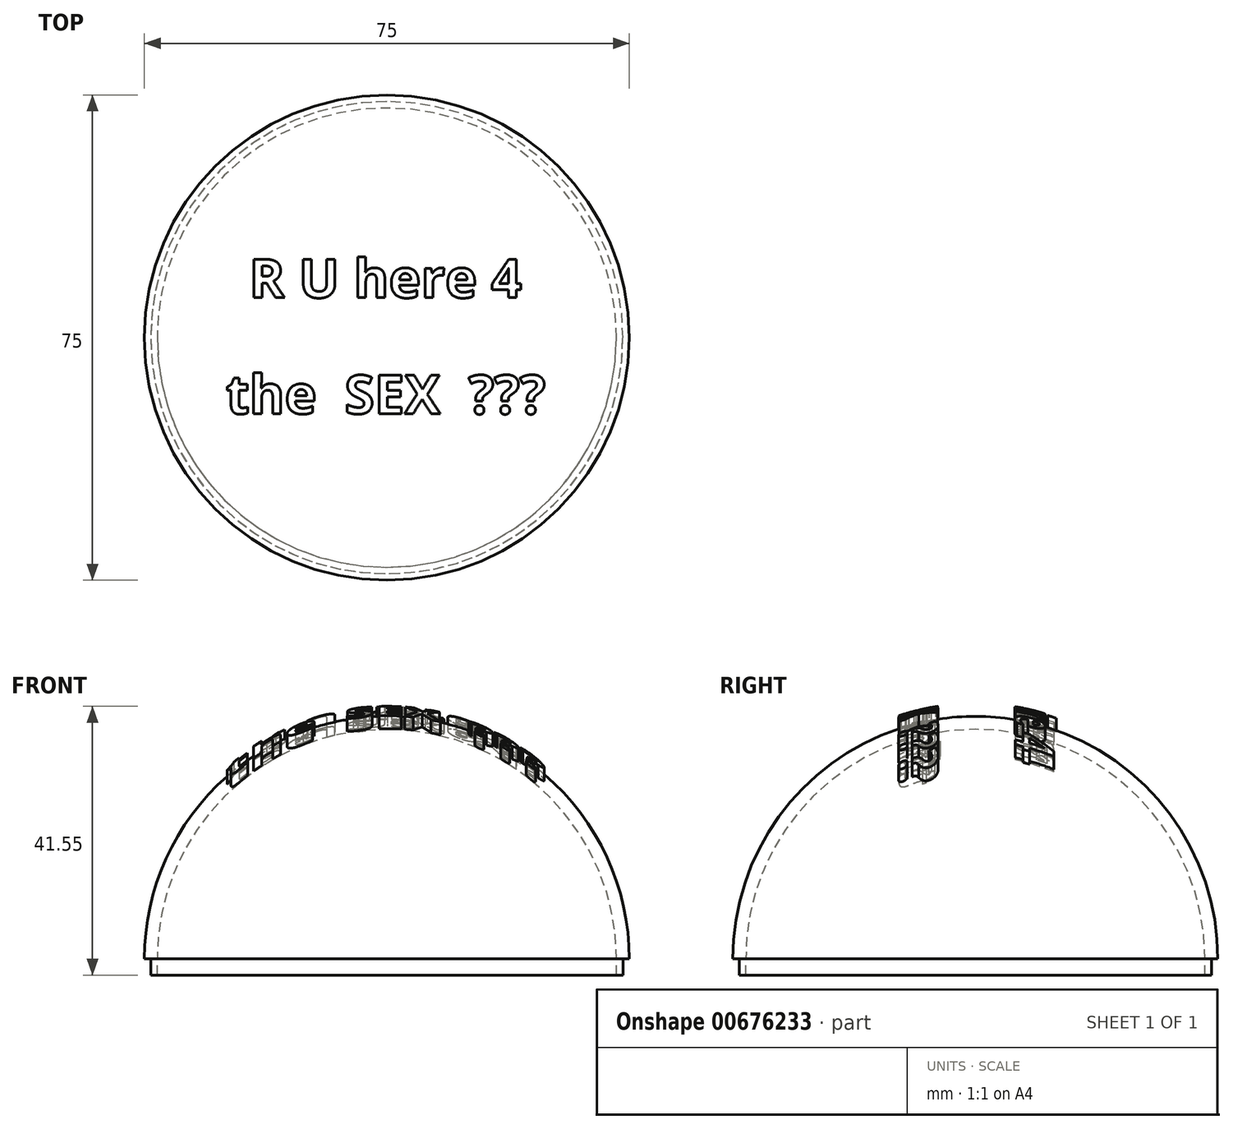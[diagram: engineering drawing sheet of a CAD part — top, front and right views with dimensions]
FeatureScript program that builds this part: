
annotation { "Feature Type Name" : "Feature", "Feature Type Description" : "" }
export const myFeature = defineFeature(function(context is Context, id is Id, definition is map)
    precondition{}
    {
        {
            var Q0;
            Q0=qCreatedBy(makeId("Front.planeOp"),FACE);
            var sketch = newSketch(context, id + "F0", { "sketchPlane" : qUnion([Q0])});
            skArc(sketch, "E0", {"start": v(37.5, 0) * mm, "mid": v(0, 37.5) * mm, "end": v(-37.5, 0) * mm});
            skArc(sketch, "E1", {"start": v(35.5, 0) * mm, "mid": v(0, 35.5) * mm, "end": v(-35.5, 0) * mm});
            skLineSegment(sketch, "E2", {"start": v(35.5, 0) * mm, "end": v(37.5, 0) * mm});
            skLineSegment(sketch, "E3", {"start": v(-37.5, 0) * mm, "end": v(-35.5, 0) * mm});
            skLineSegment(sketch, "E4", {"start": v(-37.5, 0) * mm, "end": v(42.78, 0) * mm, "construction": true});
            skLineSegment(sketch, "E5", {"start": v(36.5, 0) * mm, "end": v(36.5, 2.5) * mm});
            skLineSegment(sketch, "E6", {"start": v(36.5, 2.5) * mm, "end": v(35.41, 2.5) * mm});
            skLineSegment(sketch, "E7", {"start": v(36.5, 0) * mm, "end": v(36.5, -2.5) * mm});
            skLineSegment(sketch, "E8", {"start": v(36.5, -2.5) * mm, "end": v(35.5, -2.5) * mm});
            skLineSegment(sketch, "E9", {"start": v(35.5, 0) * mm, "end": v(35.5, -2.5) * mm});
            skSolve(sketch);
        }
        {
            var Q0;
            Q0=makeQuery(id+"F0.imprint","IMPRINT",FACE,{"disambiguationData":[TD([[makeQuery(id+"F0.imprint","IMPRINT",EDGE,{"derivedFrom":sQuery(id+"F0.wireOp",EDGE,"E0")}),1.0]])]});
            var Q1;
            {var subQ4=sQuery(id+"F0.wireOp",EDGE,"E5");Q1=makeQuery(id+"F0.imprint","IMPRINT",FACE,{"disambiguationData":[TD([[makeQuery(id+"F0.imprint","IMPRINT",EDGE,{"derivedFrom":subQ4}),1.0]])]});}
            var Q2;
            Q2=sQuery(id+"F0.wireOp",EDGE,"E4");
            revolve(context, id + "F1", {"entities" : qUnion([Q0, Q1]), "axis" : qUnion([Q2]), "revolveType" : RevolveType.SYMMETRIC, "angle" : 180 * degree});
        }
        {
            var Q0;
            Q0=qCreatedBy(makeId("Top.planeOp"),FACE);
            var sketch = newSketch(context, id + "F2", { "sketchPlane" : qUnion([Q0])});
            skText(sketch, "E10", { "text": "R U here 4", "fontName": "OpenSans-Bold.ttf"});
            skText(sketch, "E11", { "text": "the  SEX  ???", "fontName": "OpenSans-Bold.ttf"});
            const initialGuessF2  = {"E10": [-0.02129, 0.00617, 1, 0, 0.006], "E11": [-0.02488, -0.01177, 1, 0, 0.006]};
            skSetInitialGuess(sketch, initialGuessF2);
            skSolve(sketch);
        }
        {
            var Q0;
            Q0=qSketchRegion(id+"F2",true);
            var Q1;
            Q1=makeQuery(id+"F1.opRevolve","SWEPT_FACE",FACE,{"disambiguationData":[OSD([sQuery(id+"F0.wireOp",EDGE,"E0")])]});
            extrude(context, id + "F3", {"entities" : qUnion([Q0]), "operationType" : NewBodyOperationType.ADD, "endBound" : BoundingType.UP_TO_SURFACE, "depth" : 39.5 * mm, "endBoundEntityFace" : qUnion([Q1]), "hasOffset" : true, "offsetDistance" : 2 * mm, "offsetOppositeDirection" : true});
        }
        {
            var Q0;
            Q0=qSketchRegion(id+"F2",true);
            var Q1;
            {var subQ0=sQuery(id+"F0.wireOp",EDGE,"E1");Q1=makeQuery(id+"F3.boolean.opBoolean","SPLIT",FACE,{"disambiguationData":[TD([makeQuery(id+"F3.opExtrude","SWEPT_FACE",FACE,{"disambiguationData":[OSD([sQuery(id+"F2.wireOp",EDGE,"E10.sketch_text.stroke-0")])]})])],"derivedFrom":makeQuery(id+"F1.opRevolve","SWEPT_FACE",FACE,{"disambiguationData":[OSD([subQ0])]})});}
            extrude(context, id + "F4", {"entities" : qUnion([Q0]), "operationType" : NewBodyOperationType.REMOVE, "endBound" : BoundingType.UP_TO_SURFACE, "depth" : 25 * mm, "endBoundEntityFace" : qUnion([Q1]), "offsetDistance" : 25 * mm});
        }
        {
            var Q0;
            Q0=qCreatedBy(makeId("Right.planeOp"),FACE);
            var sketch = newSketch(context, id + "F5", { "sketchPlane" : qUnion([Q0])});
            skLineSegment(sketch, "E12", {"start": v(0, 42.71) * mm, "end": v(0, -17.22) * mm, "construction": true});
            skSolve(sketch);
        }
        {
            var Q0;
            {var subQ2=sQuery(id+"F0.wireOp",EDGE,"E7");Q0=makeQuery(id+"F0.imprint","IMPRINT",FACE,{"disambiguationData":[TD([[makeQuery(id+"F0.imprint","IMPRINT",EDGE,{"derivedFrom":subQ2}),-1.0]])]});}
            var Q1;
            Q1=sQuery(id+"F5.wireOp",EDGE,"E12");
            revolve(context, id + "F6", {"operationType" : NewBodyOperationType.ADD, "entities" : qUnion([Q0]), "axis" : qUnion([Q1]), "revolveType" : RevolveType.FULL});
        }
    });
